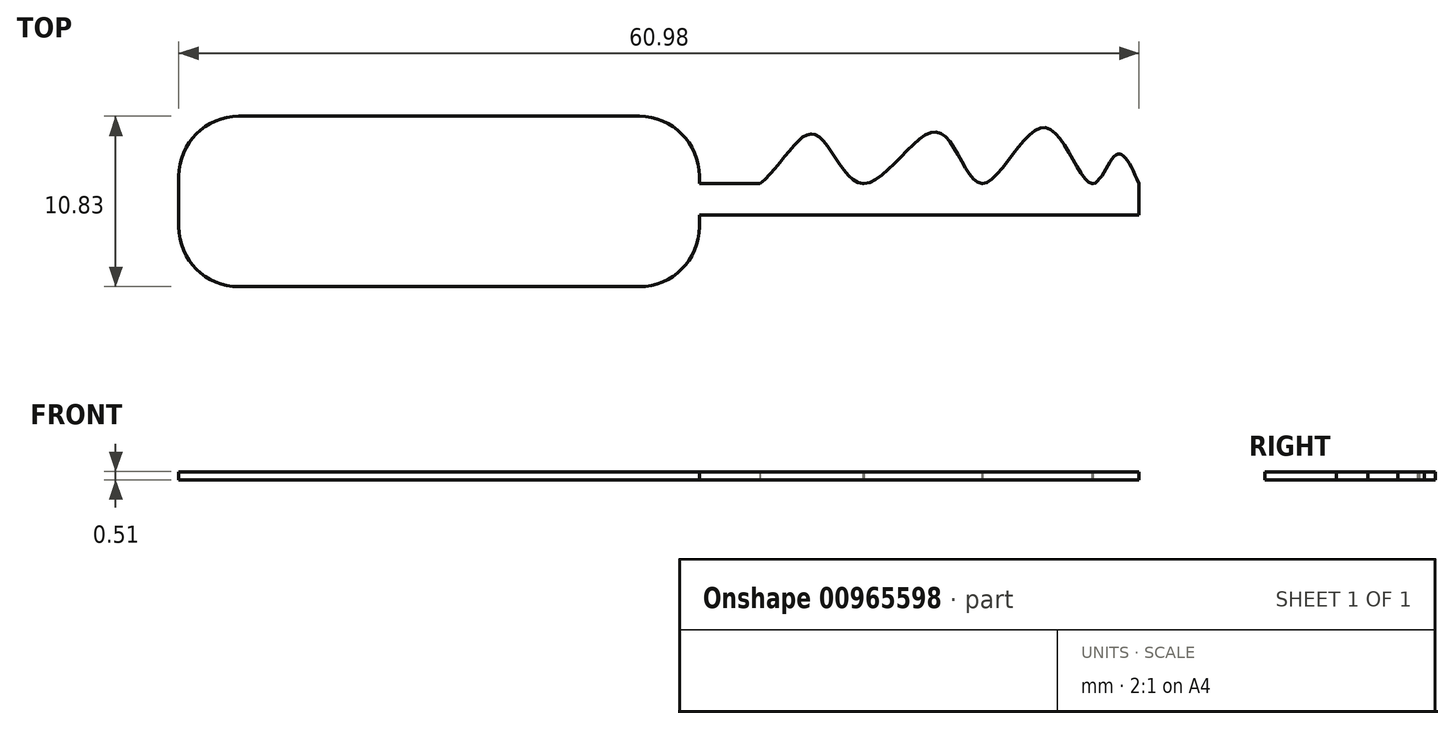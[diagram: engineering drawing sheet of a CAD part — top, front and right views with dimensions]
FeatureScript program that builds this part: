
annotation { "Feature Type Name" : "Feature", "Feature Type Description" : "" }
export const myFeature = defineFeature(function(context is Context, id is Id, definition is map)
    precondition{}
    {
        {
            var Q0;
            Q0=qCreatedBy(makeId("Top.planeOp"),FACE);
            var sketch = newSketch(context, id + "F0", { "sketchPlane" : qUnion([Q0])});
            skLineSegment(sketch, "E0.bottom", {"start": v(-17.95, 22.37) * mm, "end": v(9.97, 22.37) * mm});
            skLineSegment(sketch, "E0.top", {"start": v(-17.95, 20.38) * mm, "end": v(9.97, 20.38) * mm});
            skLineSegment(sketch, "E0.left", {"start": v(-17.95, 22.37) * mm, "end": v(-17.95, 20.38) * mm});
            skLineSegment(sketch, "E0.right", {"start": v(9.97, 22.37) * mm, "end": v(9.97, 20.38) * mm});
            skLineSegment(sketch, "E1.bottom", {"start": v(-51.01, 26.65) * mm, "end": v(-17.95, 26.65) * mm});
            skLineSegment(sketch, "E1.top", {"start": v(-51.01, 15.82) * mm, "end": v(-17.95, 15.82) * mm});
            skLineSegment(sketch, "E1.left", {"start": v(-51.01, 26.65) * mm, "end": v(-51.01, 15.82) * mm});
            skLineSegment(sketch, "E1.right", {"start": v(-17.95, 26.65) * mm, "end": v(-17.95, 15.82) * mm});
            skLineSegment(sketch, "E2", {"start": v(-17.95, 20.38) * mm, "end": v(-10.26, 20.38) * mm});
            skLineSegment(sketch, "E3", {"start": v(-10.26, 20.38) * mm, "end": v(-2.56, 20.38) * mm});
            skLineSegment(sketch, "E4", {"start": v(-2.56, 20.38) * mm, "end": v(5.13, 20.38) * mm});
            skPoint(sketch, "E5.1.internal.snap0", {"position": v(-14.1, 20.38) * mm});
            skFitSpline(sketch, "E5", {"points": [v(-17.95, 22.37) * mm, v(-14.1, 22.37) * mm, v(-10.69, 25.5) * mm, v(-7.55, 22.37) * mm, v(-2.85, 25.65) * mm, v(0, 22.37) * mm, v(3.99, 25.93) * mm, v(6.98, 22.37) * mm, v(8.55, 24.22) * mm, v(9.97, 22.37) * mm], "startDerivative": vector(37.22, -11.8) * mm, "endDerivative": vector(16.94, -37.95) * mm});
            skSolve(sketch);
        }
        {
            var Q0;
            Q0 = qSketchRegion(id + "F0", true);
            extrude(context, id + "F1", {"entities" : qUnion([Q0]), "depth" : 0.5 * mm, "offsetDistance" : 25.4 * mm});
        }
        {
            var Q0;
            Q0=makeQuery(id+"F1.opExtrude","SWEPT_EDGE",EDGE,{"disambiguationData":[OSD([sQuery(id+"F0.wireOp",EDGE,"E1.bottom"),sQuery(id+"F0.wireOp",EDGE,"E1.right")])]});
            var Q1;
            Q1=makeQuery(id+"F1.opExtrude","SWEPT_EDGE",EDGE,{"disambiguationData":[OSD([sQuery(id+"F0.wireOp",EDGE,"E1.bottom"),sQuery(id+"F0.wireOp",EDGE,"E1.left")])]});
            var Q2;
            Q2=makeQuery(id+"F1.opExtrude","SWEPT_EDGE",EDGE,{"disambiguationData":[OSD([sQuery(id+"F0.wireOp",EDGE,"E1.top"),sQuery(id+"F0.wireOp",EDGE,"E1.left")])]});
            var Q3;
            Q3=makeQuery(id+"F1.opExtrude","SWEPT_EDGE",EDGE,{"disambiguationData":[OSD([sQuery(id+"F0.wireOp",EDGE,"E1.top"),sQuery(id+"F0.wireOp",EDGE,"E1.right")])]});
            fillet(context, id + "F2", {"entities" : qUnion([Q0, Q1, Q2, Q3]), "tangentPropagation" : true, "radius" : 3.8 * mm, "defaultsChanged" : true, "vertexSettings" : [], "allowEdgeOverflow" : false});
        }
    });
